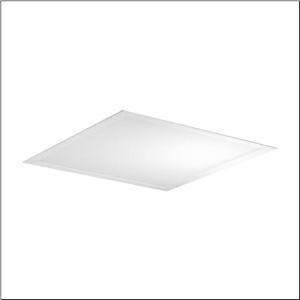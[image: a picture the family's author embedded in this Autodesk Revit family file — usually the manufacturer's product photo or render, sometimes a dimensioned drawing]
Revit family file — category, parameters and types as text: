
# Revit family: apollon_r__21_square_51mq11wd2t14_9e61
name_source: partatom
category: Lighting Fixtures
units: mm (PartAtom-declared; Revit-internal decimal feet)

## family parameters
Cut with Voids When Loaded = No
Host = Face
Light Source = No
Part Type = Normal
Room Calculation Point = No
Round Connector Dimension = Use Diameter
Shared = No

## types (1)
- --- (1 x LED 2700 K ... 6500 K, 4600 lm, 30.4 W, 4000K)
    Apparent Load = 30 VA
    CIE Flux Codes = 66 89 97 100 100
    Color Rendering = 80
    Color Temperature = 4000K
    Default Elevation = 1800 mm
    Description = Apollon® 21 square, office luminaire, primary optical cover: micro prismatic cover, of PMMA, CAT 2 (L<= 3000cd/m²), light emission: direct distribution, primary light characteristic: symmetric, installation type: lay-in mounting, LED, rated luminous flux: 4.600lm, luminous efficacy: 151lm/W, light colour: 8tw, colour temperature: 2700..6500K, with terminal, 5-pole, mains connection: 220..240V, AC/DC, 0/50..60Hz, rated input power: 30.4W, housing, of aluminium, coated, traffic white (RAL 9016), module: M625, length: 620mm, width: 620mm, height: 30mm, housing upper side, of sheet steel, galvanised, protection rating (complete): IP20, protection rating (lamp compartment, on room side): IP50, insulation class (complete): insulation class II (safety insulation), certification: CE, ENEC, impact resistance: IK03, permissible operating ambient temperature: -20..+45°C, permissible storage temperature: -40..+80°C, packaging unit: 1 piece
    Height = 0 mm  [stored 0 ft]
    Lamp = 1 x LED 2700 K ... 6500 K
    Lamp Light Flux = 4600 lm
    Lamp Power = 30.4 W
    Lamp count = 1
    Length = 620 mm
    Luminous efficacy = 151 lm/W
    Manufacturer = Siteco
    ModVariant = No
    Model = 51MQ11WD2T14
    Mounting Place = Ceiling
    Mounting Type = Recessed
    Number of Poles = 1
    OnlyDefault = Yes
    Power Factor = 1
    Product Name = Apollon® 21 square
    Product group = office luminaire | ceiling recessed
    ProductGroupID = 401
    Protection Class = Protection class II
    Protection Degree = IP 20
    RLX_Detail_Level = 1
    RLX_Emergency_Light_Flux = 0 lm
    RLX_Emergency_Type = 0
    RLX_Emergency_Type_DB = No
    RlxData = <blob elided: 12989 chars, md5=32c9bea4>
    Socket = socket
    Standby Power = 0 W
    System Light Flux = 4600 lm
    System Power = 30 W
    Type Comments = factory setting: CCT=4000K, colour temperature 4000K
    Type Image = l_1291054.jpg
    URL = http://relux.com
    VarID = @adj_026093
    Voltage = 0 V
    Weight = 0.00 kg
    Width = 620 mm

note: [stored X ft] marks values corroborated as IEEE doubles in the binary element streams (Revit-internal decimal feet)

## geometry (parser evidence)
native form markers: Sweep x10
no freeform markers — native parametric forms only
